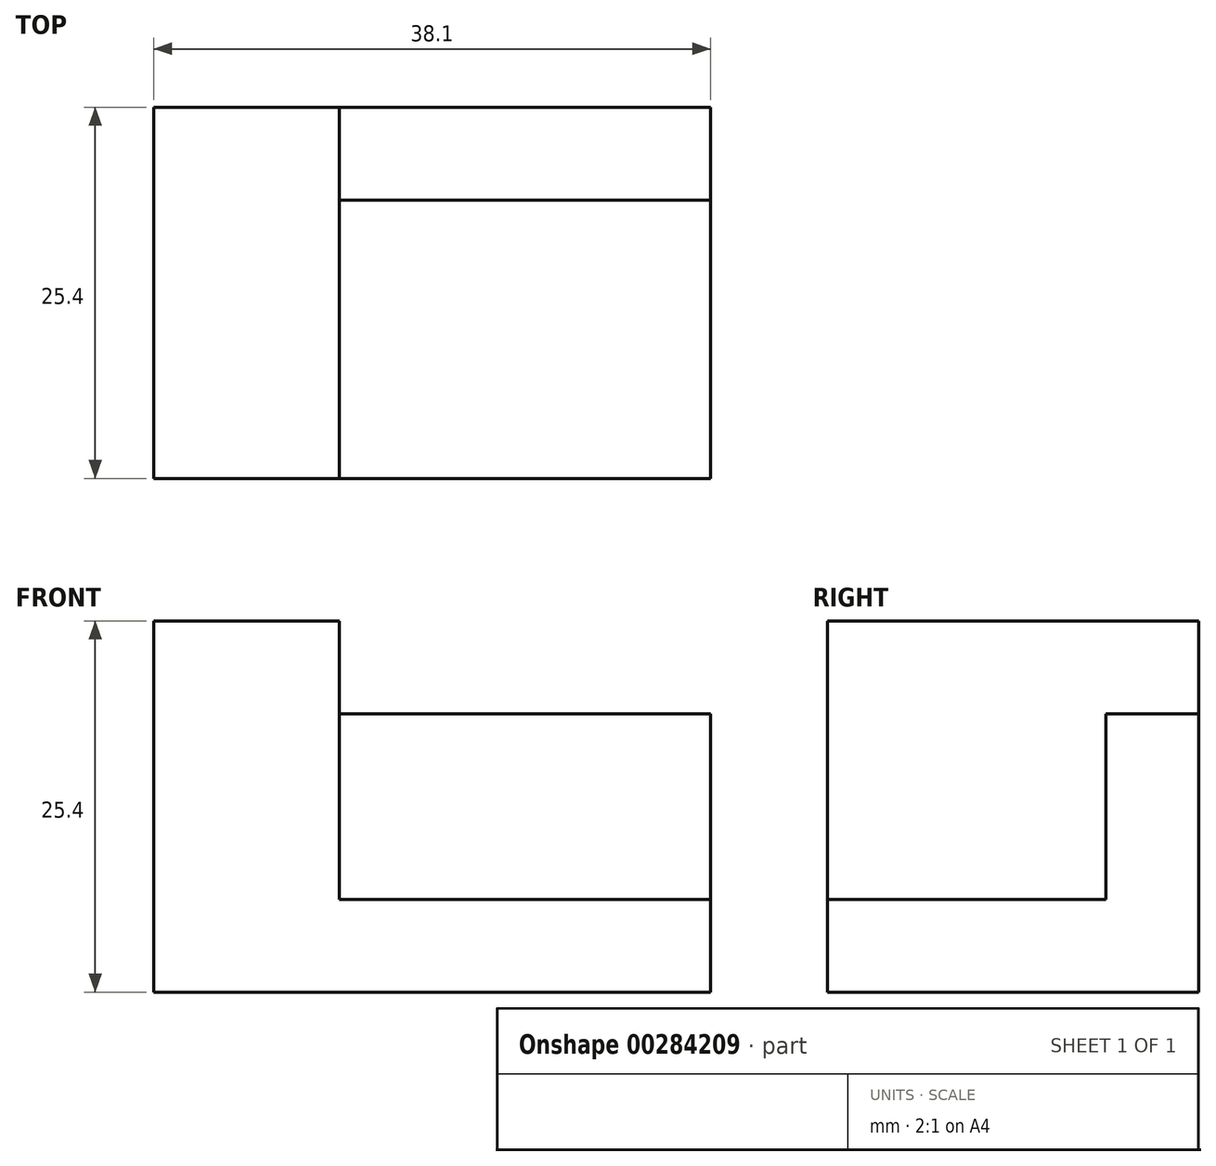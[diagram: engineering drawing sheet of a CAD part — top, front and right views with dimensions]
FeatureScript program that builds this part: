
annotation { "Feature Type Name" : "Feature", "Feature Type Description" : "" }
export const myFeature = defineFeature(function(context is Context, id is Id, definition is map)
    precondition{}
    {
        {
            var Q0;
            Q0=qCreatedBy(makeId("Front.planeOp"),FACE);
            var sketch = newSketch(context, id + "F0", { "sketchPlane" : qUnion([Q0])});
            skLineSegment(sketch, "E0", {"start": v(0, 0) * mm, "end": v(0, 25.4) * mm});
            skLineSegment(sketch, "E1", {"start": v(0, 25.4) * mm, "end": v(12.7, 25.4) * mm});
            skLineSegment(sketch, "E2", {"start": v(12.7, 25.4) * mm, "end": v(12.7, 19.05) * mm});
            skLineSegment(sketch, "E3", {"start": v(12.7, 19.05) * mm, "end": v(38.1, 19.05) * mm});
            skLineSegment(sketch, "E4", {"start": v(38.1, 19.05) * mm, "end": v(38.1, 0) * mm});
            skLineSegment(sketch, "E5", {"start": v(38.1, 0) * mm, "end": v(0, 0) * mm});
            skSolve(sketch);
        }
        {
            var Q0;
            Q0=makeQuery(id+"F0.imprint","IMPRINT",FACE,{"disambiguationData":[TD([[makeQuery(id+"F0.imprint","IMPRINT",EDGE,{"derivedFrom":sQuery(id+"F0.wireOp",EDGE,"E0")}),-1.0]])]});
            extrude(context, id + "F1", {"entities" : qUnion([Q0]), "depth" : 25.4 * mm});
        }
        {
            var Q0;
            Q0=makeQuery(id+"F1.opExtrude","CAP_FACE",FACE,{"disambiguationData":[OSD([sQuery(id+"F0.wireOp",EDGE,"E0"),sQuery(id+"F0.wireOp",EDGE,"E1"),sQuery(id+"F0.wireOp",EDGE,"E2"),sQuery(id+"F0.wireOp",EDGE,"E3"),sQuery(id+"F0.wireOp",EDGE,"E4"),sQuery(id+"F0.wireOp",EDGE,"E5")])],"isStart":false});
            var sketch = newSketch(context, id + "F2", { "sketchPlane" : qUnion([Q0])});
            skLineSegment(sketch, "E6.bottom", {"start": v(12.7, 19.05) * mm, "end": v(38.1, 19.05) * mm});
            skLineSegment(sketch, "E6.top", {"start": v(12.7, 6.35) * mm, "end": v(38.1, 6.35) * mm});
            skLineSegment(sketch, "E6.left", {"start": v(12.7, 19.05) * mm, "end": v(12.7, 6.35) * mm});
            skLineSegment(sketch, "E6.right", {"start": v(38.1, 19.05) * mm, "end": v(38.1, 6.35) * mm});
            skSolve(sketch);
        }
        {
            var Q0;
            Q0=makeQuery(id+"F2.imprint","IMPRINT",FACE,{"disambiguationData":[TD([[makeQuery(id+"F2.imprint","IMPRINT",EDGE,{"derivedFrom":sQuery(id+"F2.wireOp",EDGE,"E6.bottom")}),-1.0]])]});
            extrude(context, id + "F3", {"entities" : qUnion([Q0]), "operationType" : NewBodyOperationType.REMOVE, "oppositeDirection" : true, "depth" : 19.05 * mm});
        }
    });
